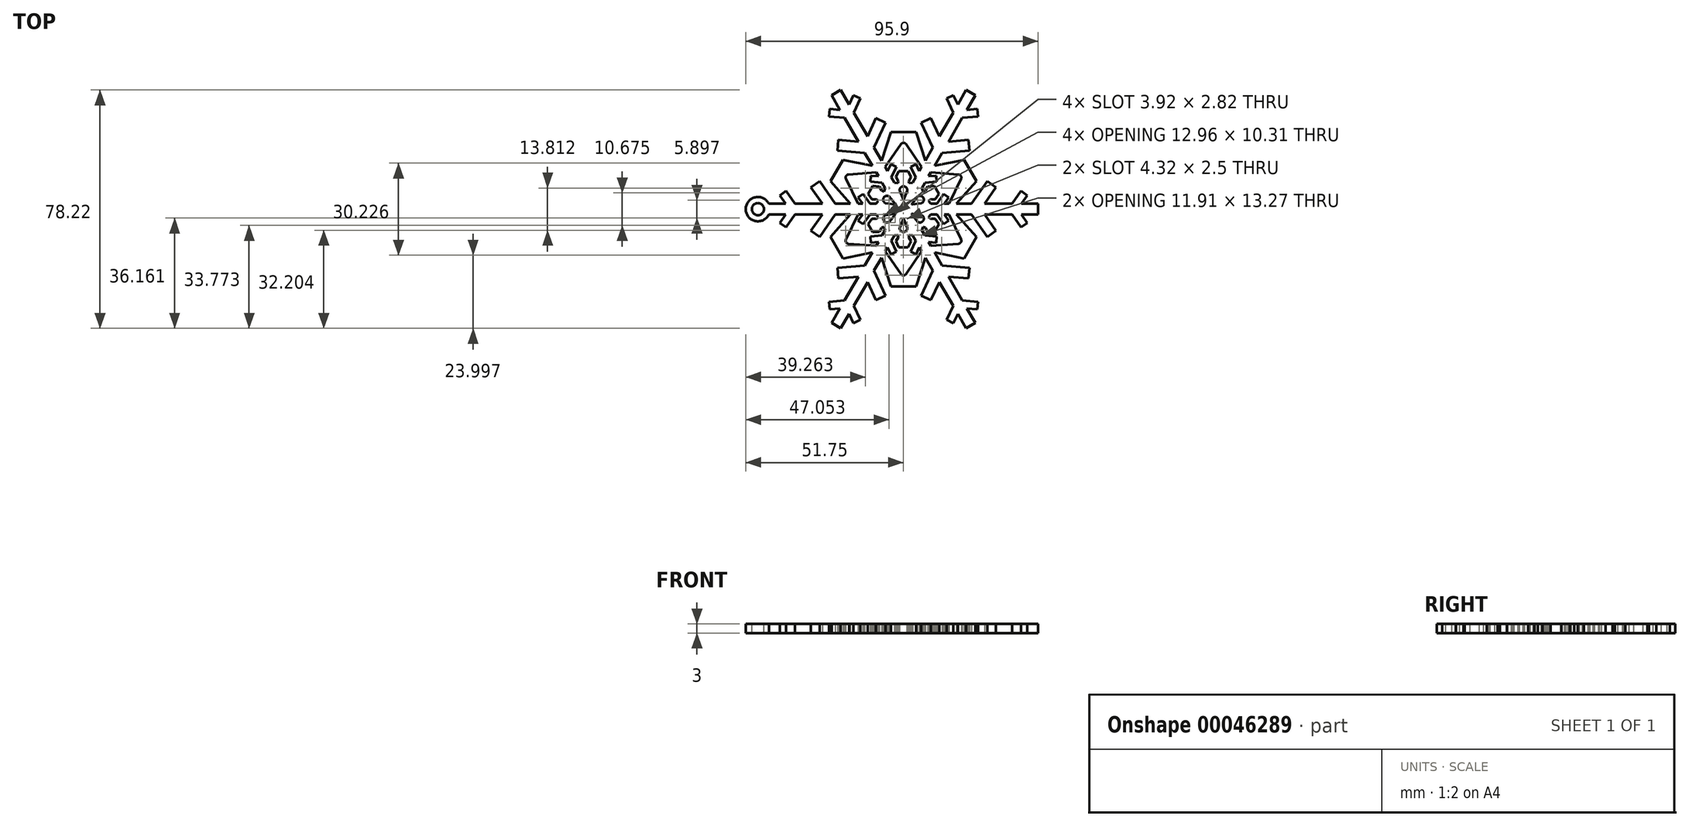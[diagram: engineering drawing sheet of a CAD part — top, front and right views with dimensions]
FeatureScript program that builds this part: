
annotation { "Feature Type Name" : "Feature", "Feature Type Description" : "" }
export const myFeature = defineFeature(function(context is Context, id is Id, definition is map)
    precondition{}
    {
        {
            var Q0;
            Q0=qCreatedBy(makeId("Top.planeOp"),FACE);
            var sketch = newSketch(context, id + "F0", { "sketchPlane" : qUnion([Q0])});
            skLineSegment(sketch, "E0.bottom", {"start": v(-43.7, 44.8) * mm, "end": v(41.1, 44.8) * mm});
            skLineSegment(sketch, "E0.top", {"start": v(-43.7, -40) * mm, "end": v(41.1, -40) * mm});
            skLineSegment(sketch, "E0.left", {"start": v(-43.7, 44.8) * mm, "end": v(-43.7, -40) * mm});
            skLineSegment(sketch, "E0.right", {"start": v(41.1, 44.8) * mm, "end": v(41.1, -40) * mm});
            skLineSegment(sketch, "E1", {"start": v(-44.15, 0) * mm, "end": v(-44.15, 1.75) * mm});
            skLineSegment(sketch, "E2", {"start": v(-44.15, 1.75) * mm, "end": v(-38.65, 1.75) * mm});
            skLineSegment(sketch, "E3", {"start": v(-38.65, 1.75) * mm, "end": v(-40.58, 4.5) * mm});
            skLineSegment(sketch, "E4", {"start": v(-40.58, 4.5) * mm, "end": v(-38.53, 5.94) * mm});
            skLineSegment(sketch, "E5", {"start": v(-38.53, 5.94) * mm, "end": v(-35.6, 1.75) * mm});
            skLineSegment(sketch, "E6", {"start": v(-35.6, 1.75) * mm, "end": v(-26.6, 1.75) * mm});
            skLineSegment(sketch, "E7", {"start": v(-26.6, 1.75) * mm, "end": v(-30.36, 7.13) * mm});
            skLineSegment(sketch, "E8", {"start": v(-30.36, 7.13) * mm, "end": v(-27.49, 9.13) * mm});
            skLineSegment(sketch, "E9", {"start": v(-27.49, 9.13) * mm, "end": v(-22.34, 1.75) * mm});
            skLineSegment(sketch, "E10", {"start": v(-22.34, 1.75) * mm, "end": v(-17.4, 1.75) * mm});
            skLineSegment(sketch, "E11", {"start": v(-14.94, 1.75) * mm, "end": v(-13.44, 1.75) * mm});
            skLineSegment(sketch, "E12", {"start": v(-13.44, 1.75) * mm, "end": v(-14.87, 3.8) * mm});
            skLineSegment(sketch, "E13", {"start": v(-14.87, 3.8) * mm, "end": v(-13.23, 4.94) * mm});
            skLineSegment(sketch, "E14", {"start": v(-13.23, 4.94) * mm, "end": v(-11, 1.75) * mm});
            skLineSegment(sketch, "E15", {"start": v(0, 0) * mm, "end": v(-44.15, 0) * mm, "construction": true});
            skLineSegment(sketch, "E16", {"start": v(-11, 1.75) * mm, "end": v(-8.98, 1.75) * mm});
            skLineSegment(sketch, "E17", {"start": v(0, 0) * mm, "end": v(-10.85, 6.27) * mm});
            skLineSegment(sketch, "E18", {"start": v(-8.98, 1.75) * mm, "end": v(-8.24, 2.67) * mm});
            skLineSegment(sketch, "E19", {"start": v(-8.24, 2.67) * mm, "end": v(-8.84, 3.15) * mm});
            skLineSegment(sketch, "E20", {"start": v(-8.84, 3.15) * mm, "end": v(-10.37, 3.15) * mm});
            skLineSegment(sketch, "E21", {"start": v(-10.37, 3.15) * mm, "end": v(-11.62, 4.94) * mm});
            skLineSegment(sketch, "E22", {"start": v(-11.62, 4.94) * mm, "end": v(-10.85, 6.27) * mm});
            skLineSegment(sketch, "E23", {"start": v(-10.85, 6.27) * mm, "end": v(-31.84, 18.38) * mm, "construction": true});
            skLineSegment(sketch, "E24", {"start": v(-23.98, 9.13) * mm, "end": v(-21.94, 12.67) * mm});
            skLineSegment(sketch, "E25", {"start": v(-14.94, 1.75) * mm, "end": v(-19.5, 11.26) * mm});
            skLineSegment(sketch, "E26", {"start": v(-23.98, 9.13) * mm, "end": v(-17.4, 1.75) * mm});
            skLineSegment(sketch, "E27", {"start": v(-21.94, 12.67) * mm, "end": v(-19.5, 11.26) * mm});
            skLineSegment(sketch, "E28.MirrorCS", {"start": v(0, 0) * mm, "end": v(-10.85, -6.27) * mm});
            skLineSegment(sketch, "E29.MirrorCS", {"start": v(-44.15, 0) * mm, "end": v(-44.15, -1.75) * mm});
            skLineSegment(sketch, "E30.MirrorCS", {"start": v(-14.94, -1.75) * mm, "end": v(-13.44, -1.75) * mm});
            skLineSegment(sketch, "E31.MirrorCS", {"start": v(-11.62, -4.94) * mm, "end": v(-10.85, -6.27) * mm});
            skLineSegment(sketch, "E32.MirrorCS", {"start": v(-14.87, -3.8) * mm, "end": v(-13.23, -4.94) * mm});
            skLineSegment(sketch, "E33.MirrorCS", {"start": v(-8.98, -1.75) * mm, "end": v(-8.24, -2.67) * mm});
            skLineSegment(sketch, "E34.MirrorCS", {"start": v(-8.84, -3.15) * mm, "end": v(-10.37, -3.15) * mm});
            skLineSegment(sketch, "E35.MirrorCS", {"start": v(-8.24, -2.67) * mm, "end": v(-8.84, -3.15) * mm});
            skLineSegment(sketch, "E36.MirrorCS", {"start": v(-14.94, -1.75) * mm, "end": v(-19.5, -11.26) * mm});
            skLineSegment(sketch, "E37.MirrorCS", {"start": v(-27.49, -9.13) * mm, "end": v(-22.34, -1.75) * mm});
            skLineSegment(sketch, "E38.MirrorCS", {"start": v(-21.94, -12.67) * mm, "end": v(-19.5, -11.26) * mm});
            skLineSegment(sketch, "E39.MirrorCS", {"start": v(-23.98, -9.13) * mm, "end": v(-21.94, -12.67) * mm});
            skLineSegment(sketch, "E40.MirrorCS", {"start": v(-11, -1.75) * mm, "end": v(-8.98, -1.75) * mm});
            skLineSegment(sketch, "E41.MirrorCS", {"start": v(-38.53, -5.94) * mm, "end": v(-35.6, -1.75) * mm});
            skLineSegment(sketch, "E42.MirrorCS", {"start": v(-40.58, -4.5) * mm, "end": v(-38.53, -5.94) * mm});
            skLineSegment(sketch, "E43.MirrorCS", {"start": v(-38.65, -1.75) * mm, "end": v(-40.58, -4.5) * mm});
            skLineSegment(sketch, "E44.MirrorCS", {"start": v(-44.15, -1.75) * mm, "end": v(-38.65, -1.75) * mm});
            skLineSegment(sketch, "E45.MirrorCS", {"start": v(-23.98, -9.13) * mm, "end": v(-17.4, -1.75) * mm});
            skLineSegment(sketch, "E46.MirrorCS", {"start": v(-30.36, -7.13) * mm, "end": v(-27.49, -9.13) * mm});
            skLineSegment(sketch, "E47.MirrorCS", {"start": v(-26.6, -1.75) * mm, "end": v(-30.36, -7.13) * mm});
            skLineSegment(sketch, "E48.MirrorCS", {"start": v(-35.6, -1.75) * mm, "end": v(-26.6, -1.75) * mm});
            skLineSegment(sketch, "E49.MirrorCS", {"start": v(-22.34, -1.75) * mm, "end": v(-17.4, -1.75) * mm});
            skLineSegment(sketch, "E50.MirrorCS", {"start": v(-13.44, -1.75) * mm, "end": v(-14.87, -3.8) * mm});
            skLineSegment(sketch, "E51.MirrorCS", {"start": v(-10.37, -3.15) * mm, "end": v(-11.62, -4.94) * mm});
            skLineSegment(sketch, "E52.MirrorCS", {"start": v(-13.23, -4.94) * mm, "end": v(-11, -1.75) * mm});
            skSolve(sketch);
        }
        {
            var Q0;
            Q0=makeQuery(id+"F0.imprint","IMPRINT",FACE,{"disambiguationData":[TD([[makeQuery(id+"F0.imprint","IMPRINT",EDGE,{"derivedFrom":sQuery(id+"F0.wireOp",EDGE,"E1")}),-1.0]])]});
            var Q1;
            {var subQ0=sQuery(id+"F0.wireOp",EDGE,"E3");Q1=makeQuery(id+"F0.imprint","IMPRINT",FACE,{"disambiguationData":[TD([[makeQuery(id+"F0.imprint","IMPRINT",EDGE,{"derivedFrom":subQ0}),-1.0]])]});}
            extrude(context, id + "F1", {"entities" : qUnion([Q0, Q1]), "endBound" : BoundingType.SYMMETRIC, "depth" : 3 * mm});
        }
        {
            var Q0;
            Q0=qCreatedBy(makeId("Right.planeOp"),FACE);
            var sketch = newSketch(context, id + "F2", { "sketchPlane" : qUnion([Q0])});
            skLineSegment(sketch, "E53", {"start": v(0, 0) * mm, "end": v(0, -43.45) * mm, "construction": true});
            skSolve(sketch);
        }
        {
            var Q0;
            Q0=makeQuery(id+"F1.opExtrude","SWEPT_BODY",BODY,{"disambiguationData":[OSD([sQuery(id+"F0.wireOp",EDGE,"E1"),sQuery(id+"F0.wireOp",EDGE,"E2"),sQuery(id+"F0.wireOp",EDGE,"E3"),sQuery(id+"F0.wireOp",EDGE,"E4"),sQuery(id+"F0.wireOp",EDGE,"E5"),sQuery(id+"F0.wireOp",EDGE,"E6"),sQuery(id+"F0.wireOp",EDGE,"E7"),sQuery(id+"F0.wireOp",EDGE,"E8"),sQuery(id+"F0.wireOp",EDGE,"E9"),sQuery(id+"F0.wireOp",EDGE,"E10"),sQuery(id+"F0.wireOp",EDGE,"189a7a4e-f39c-4bfd-b122-43a29ca94680"),sQuery(id+"F0.wireOp",EDGE,"67050dc1-3990-4a49-9707-dffdccfb30a0"),sQuery(id+"F0.wireOp",EDGE,"437a0215-fb6c-4063-ad75-b84b83856d58"),sQuery(id+"F0.wireOp",EDGE,"E11"),sQuery(id+"F0.wireOp",EDGE,"E12"),sQuery(id+"F0.wireOp",EDGE,"E13"),sQuery(id+"F0.wireOp",EDGE,"E14"),sQuery(id+"F0.wireOp",EDGE,"5e9898c1-a996-4e9f-834a-20b7154747a1"),sQuery(id+"F0.wireOp",EDGE,"4f175b08-8b9f-4015-be58-81c3dce13333"),sQuery(id+"F0.wireOp",EDGE,"3166d6ec-2b74-46b0-8a25-8ff819b97b050.MirrorCS"),sQuery(id+"F0.wireOp",EDGE,"3166d6ec-2b74-46b0-8a25-8ff819b97b051.MirrorCS"),sQuery(id+"F0.wireOp",EDGE,"3166d6ec-2b74-46b0-8a25-8ff819b97b052.MirrorCS"),sQuery(id+"F0.wireOp",EDGE,"3166d6ec-2b74-46b0-8a25-8ff819b97b053.MirrorCS"),sQuery(id+"F0.wireOp",EDGE,"3166d6ec-2b74-46b0-8a25-8ff819b97b054.MirrorCS"),sQuery(id+"F0.wireOp",EDGE,"3166d6ec-2b74-46b0-8a25-8ff819b97b055.MirrorCS"),sQuery(id+"F0.wireOp",EDGE,"3166d6ec-2b74-46b0-8a25-8ff819b97b056.MirrorCS"),sQuery(id+"F0.wireOp",EDGE,"3166d6ec-2b74-46b0-8a25-8ff819b97b057.MirrorCS"),sQuery(id+"F0.wireOp",EDGE,"3166d6ec-2b74-46b0-8a25-8ff819b97b058.MirrorCS"),sQuery(id+"F0.wireOp",EDGE,"3166d6ec-2b74-46b0-8a25-8ff819b97b059.MirrorCS"),sQuery(id+"F0.wireOp",EDGE,"3166d6ec-2b74-46b0-8a25-8ff819b97b0510.MirrorCS"),sQuery(id+"F0.wireOp",EDGE,"3166d6ec-2b74-46b0-8a25-8ff819b97b0511.MirrorCS"),sQuery(id+"F0.wireOp",EDGE,"3166d6ec-2b74-46b0-8a25-8ff819b97b0512.MirrorCS"),sQuery(id+"F0.wireOp",EDGE,"3166d6ec-2b74-46b0-8a25-8ff819b97b0513.MirrorCS"),sQuery(id+"F0.wireOp",EDGE,"3166d6ec-2b74-46b0-8a25-8ff819b97b0514.MirrorCS"),sQuery(id+"F0.wireOp",EDGE,"3166d6ec-2b74-46b0-8a25-8ff819b97b0515.MirrorCS"),sQuery(id+"F0.wireOp",EDGE,"3166d6ec-2b74-46b0-8a25-8ff819b97b0516.MirrorCS"),sQuery(id+"F0.wireOp",EDGE,"3166d6ec-2b74-46b0-8a25-8ff819b97b0517.MirrorCS"),sQuery(id+"F0.wireOp",EDGE,"3166d6ec-2b74-46b0-8a25-8ff819b97b0518.MirrorCS")])]});
            var Q1;
            Q1=sQuery(id+"F2.wireOp",EDGE,"E53");
            circularPattern(context, id + "F3", {"operationType" : NewBodyOperationType.ADD, "entities" : qUnion([Q0]), "axis" : qUnion([Q1]), "angle" : 60 * degree, "instanceCount" : 6});
        }
        {
            var Q0;
            {var subQ0=makeQuery(id+"F1.opExtrude","CAP_FACE",FACE,{"disambiguationData":[OSD([sQuery(id+"F0.wireOp",EDGE,"E1"),sQuery(id+"F0.wireOp",EDGE,"E2"),sQuery(id+"F0.wireOp",EDGE,"E3"),sQuery(id+"F0.wireOp",EDGE,"E4"),sQuery(id+"F0.wireOp",EDGE,"E5"),sQuery(id+"F0.wireOp",EDGE,"E6"),sQuery(id+"F0.wireOp",EDGE,"E7"),sQuery(id+"F0.wireOp",EDGE,"E8"),sQuery(id+"F0.wireOp",EDGE,"E9"),sQuery(id+"F0.wireOp",EDGE,"E10"),sQuery(id+"F0.wireOp",EDGE,"189a7a4e-f39c-4bfd-b122-43a29ca94680"),sQuery(id+"F0.wireOp",EDGE,"67050dc1-3990-4a49-9707-dffdccfb30a0"),sQuery(id+"F0.wireOp",EDGE,"437a0215-fb6c-4063-ad75-b84b83856d58"),sQuery(id+"F0.wireOp",EDGE,"E11"),sQuery(id+"F0.wireOp",EDGE,"E12"),sQuery(id+"F0.wireOp",EDGE,"E13"),sQuery(id+"F0.wireOp",EDGE,"E14"),sQuery(id+"F0.wireOp",EDGE,"E16"),sQuery(id+"F0.wireOp",EDGE,"E17"),sQuery(id+"F0.wireOp",EDGE,"E18"),sQuery(id+"F0.wireOp",EDGE,"E19"),sQuery(id+"F0.wireOp",EDGE,"E20"),sQuery(id+"F0.wireOp",EDGE,"E21"),sQuery(id+"F0.wireOp",EDGE,"E22"),sQuery(id+"F0.wireOp",EDGE,"0c32c283-354d-45ec-8926-575daeb4bd260.MirrorCS"),sQuery(id+"F0.wireOp",EDGE,"0c32c283-354d-45ec-8926-575daeb4bd261.MirrorCS"),sQuery(id+"F0.wireOp",EDGE,"0c32c283-354d-45ec-8926-575daeb4bd262.MirrorCS"),sQuery(id+"F0.wireOp",EDGE,"0c32c283-354d-45ec-8926-575daeb4bd263.MirrorCS"),sQuery(id+"F0.wireOp",EDGE,"0c32c283-354d-45ec-8926-575daeb4bd264.MirrorCS"),sQuery(id+"F0.wireOp",EDGE,"0c32c283-354d-45ec-8926-575daeb4bd265.MirrorCS"),sQuery(id+"F0.wireOp",EDGE,"0c32c283-354d-45ec-8926-575daeb4bd266.MirrorCS"),sQuery(id+"F0.wireOp",EDGE,"0c32c283-354d-45ec-8926-575daeb4bd267.MirrorCS"),sQuery(id+"F0.wireOp",EDGE,"0c32c283-354d-45ec-8926-575daeb4bd268.MirrorCS"),sQuery(id+"F0.wireOp",EDGE,"0c32c283-354d-45ec-8926-575daeb4bd269.MirrorCS"),sQuery(id+"F0.wireOp",EDGE,"0c32c283-354d-45ec-8926-575daeb4bd2610.MirrorCS"),sQuery(id+"F0.wireOp",EDGE,"0c32c283-354d-45ec-8926-575daeb4bd2611.MirrorCS"),sQuery(id+"F0.wireOp",EDGE,"0c32c283-354d-45ec-8926-575daeb4bd2612.MirrorCS"),sQuery(id+"F0.wireOp",EDGE,"0c32c283-354d-45ec-8926-575daeb4bd2613.MirrorCS"),sQuery(id+"F0.wireOp",EDGE,"0c32c283-354d-45ec-8926-575daeb4bd2614.MirrorCS"),sQuery(id+"F0.wireOp",EDGE,"0c32c283-354d-45ec-8926-575daeb4bd2615.MirrorCS"),sQuery(id+"F0.wireOp",EDGE,"0c32c283-354d-45ec-8926-575daeb4bd2616.MirrorCS"),sQuery(id+"F0.wireOp",EDGE,"0c32c283-354d-45ec-8926-575daeb4bd2617.MirrorCS"),sQuery(id+"F0.wireOp",EDGE,"0c32c283-354d-45ec-8926-575daeb4bd2618.MirrorCS"),sQuery(id+"F0.wireOp",EDGE,"0c32c283-354d-45ec-8926-575daeb4bd2619.MirrorCS"),sQuery(id+"F0.wireOp",EDGE,"0c32c283-354d-45ec-8926-575daeb4bd2620.MirrorCS"),sQuery(id+"F0.wireOp",EDGE,"0c32c283-354d-45ec-8926-575daeb4bd2621.MirrorCS"),sQuery(id+"F0.wireOp",EDGE,"0c32c283-354d-45ec-8926-575daeb4bd2622.MirrorCS"),sQuery(id+"F0.wireOp",EDGE,"0c32c283-354d-45ec-8926-575daeb4bd2623.MirrorCS")])],"isStart":false});Q0=makeQuery(id+"F3.boolean.opBoolean","MERGE",FACE,{"derivedFrom":[subQ0,makeQuery(id+"F3.opPattern","COPY",FACE,{"derivedFrom":subQ0,"instanceName":"1"}),makeQuery(id+"F3.opPattern","COPY",FACE,{"derivedFrom":subQ0,"instanceName":"2"}),makeQuery(id+"F3.opPattern","COPY",FACE,{"derivedFrom":subQ0,"instanceName":"3"}),makeQuery(id+"F3.opPattern","COPY",FACE,{"derivedFrom":subQ0,"instanceName":"4"}),makeQuery(id+"F3.opPattern","COPY",FACE,{"derivedFrom":subQ0,"instanceName":"5"})]});}
            var sketch = newSketch(context, id + "F4", { "sketchPlane" : qUnion([Q0])});
            skLineSegment(sketch, "E54", {"start": v(0, 0) * mm, "end": v(-10.85, 6.27) * mm, "construction": true});
            skLineSegment(sketch, "E55", {"start": v(-6.5, 3.75) * mm, "end": v(-2.6, 1.5) * mm, "construction": true});
            skLineSegment(sketch, "E56", {"start": v(-5.87, 1.94) * mm, "end": v(-2.6, 1.5) * mm});
            skLineSegment(sketch, "E57.MirrorCS", {"start": v(-4.62, 4.1) * mm, "end": v(-2.6, 1.5) * mm});
            skLineSegment(sketch, "E58", {"start": v(-5.87, 1.94) * mm, "end": v(-4.62, 4.1) * mm, "construction": true});
            skArc(sketch, "E59", {"start": v(-4.62, 4.1) * mm, "mid": v(-6.5, 3.75) * mm, "end": v(-5.87, 1.94) * mm});
            skSolve(sketch);
        }
        {
            var Q0;
            Q0=makeQuery(id+"F4.imprint","IMPRINT",FACE,{"disambiguationData":[TD([[makeQuery(id+"F4.imprint","IMPRINT",EDGE,{"derivedFrom":sQuery(id+"F4.wireOp",EDGE,"980073ca-cf30-472a-b92e-9ee7ff5da41c")}),1.0]])]});
            var Q1;
            Q1=makeQuery(id+"F4.imprint","IMPRINT",FACE,{"disambiguationData":[TD([[makeQuery(id+"F4.imprint","IMPRINT",EDGE,{"derivedFrom":sQuery(id+"F4.wireOp",EDGE,"E56")}),1.0]])]});
            extrude(context, id + "F5", {"entities" : qUnion([Q0, Q1]), "operationType" : NewBodyOperationType.REMOVE, "endBound" : BoundingType.UP_TO_NEXT, "oppositeDirection" : true, "depth" : 25 * mm});
        }
        {
            var Q0;
            Q0=makeQuery(id+"F5.boolean.opBoolean","COPY",EDGE,{"derivedFrom":makeQuery(id+"F5.opExtrude","SWEPT_EDGE",EDGE,{"disambiguationData":[OSD([sQuery(id+"F4.wireOp",EDGE,"E56"),sQuery(id+"F4.wireOp",EDGE,"E57.MirrorCS")])]})});
            fillet(context, id + "F6", {"entities" : qUnion([Q0]), "radius" : 0.1 * mm, "tangentPropagation" : true, "allowEdgeOverflow" : false});
        }
        {
            var Q0;
            Q0=makeQuery(id+"F5.boolean.opBoolean","COPY",FACE,{"derivedFrom":makeQuery(id+"F5.opExtrude","SWEPT_FACE",FACE,{"disambiguationData":[OSD([sQuery(id+"F4.wireOp",EDGE,"E59")])]})});
            var Q1;
            Q1=makeQuery(id+"F5.boolean.opBoolean","COPY",FACE,{"derivedFrom":makeQuery(id+"F5.opExtrude","SWEPT_FACE",FACE,{"disambiguationData":[OSD([sQuery(id+"F4.wireOp",EDGE,"E56")])]})});
            var Q2;
            Q2=makeQuery(id+"F5.boolean.opBoolean","COPY",FACE,{"derivedFrom":makeQuery(id+"F5.opExtrude","SWEPT_FACE",FACE,{"disambiguationData":[OSD([sQuery(id+"F4.wireOp",EDGE,"E57.MirrorCS")])]})});
            var Q3;
            Q3=makeQuery(id+"F6.opFillet","BLEND_FACE",FACE,{"disambiguationData":[OSD([sQuery(id+"F4.wireOp",EDGE,"E56"),sQuery(id+"F4.wireOp",EDGE,"E57.MirrorCS")])]});
            var Q4;
            Q4=sQuery(id+"F2.wireOp",EDGE,"E53");
            circularPattern(context, id + "F7", {"faces" : qUnion([Q0, Q1, Q2, Q3]), "axis" : qUnion([Q4]), "angle" : 60 * degree, "instanceCount" : 6, "patternType" : PatternType.FACE});
        }
        {
            var Q0;
            {var subQ0=makeQuery(id+"F1.opExtrude","CAP_FACE",FACE,{"disambiguationData":[OSD([sQuery(id+"F0.wireOp",EDGE,"E1"),sQuery(id+"F0.wireOp",EDGE,"E2"),sQuery(id+"F0.wireOp",EDGE,"E3"),sQuery(id+"F0.wireOp",EDGE,"E4"),sQuery(id+"F0.wireOp",EDGE,"E5"),sQuery(id+"F0.wireOp",EDGE,"E6"),sQuery(id+"F0.wireOp",EDGE,"E7"),sQuery(id+"F0.wireOp",EDGE,"E8"),sQuery(id+"F0.wireOp",EDGE,"E9"),sQuery(id+"F0.wireOp",EDGE,"E10"),sQuery(id+"F0.wireOp",EDGE,"189a7a4e-f39c-4bfd-b122-43a29ca94680"),sQuery(id+"F0.wireOp",EDGE,"67050dc1-3990-4a49-9707-dffdccfb30a0"),sQuery(id+"F0.wireOp",EDGE,"437a0215-fb6c-4063-ad75-b84b83856d58"),sQuery(id+"F0.wireOp",EDGE,"E11"),sQuery(id+"F0.wireOp",EDGE,"E12"),sQuery(id+"F0.wireOp",EDGE,"E13"),sQuery(id+"F0.wireOp",EDGE,"E14"),sQuery(id+"F0.wireOp",EDGE,"E16"),sQuery(id+"F0.wireOp",EDGE,"E17"),sQuery(id+"F0.wireOp",EDGE,"E18"),sQuery(id+"F0.wireOp",EDGE,"E19"),sQuery(id+"F0.wireOp",EDGE,"E20"),sQuery(id+"F0.wireOp",EDGE,"E21"),sQuery(id+"F0.wireOp",EDGE,"E22"),sQuery(id+"F0.wireOp",EDGE,"0c32c283-354d-45ec-8926-575daeb4bd260.MirrorCS"),sQuery(id+"F0.wireOp",EDGE,"0c32c283-354d-45ec-8926-575daeb4bd261.MirrorCS"),sQuery(id+"F0.wireOp",EDGE,"0c32c283-354d-45ec-8926-575daeb4bd262.MirrorCS"),sQuery(id+"F0.wireOp",EDGE,"0c32c283-354d-45ec-8926-575daeb4bd263.MirrorCS"),sQuery(id+"F0.wireOp",EDGE,"0c32c283-354d-45ec-8926-575daeb4bd264.MirrorCS"),sQuery(id+"F0.wireOp",EDGE,"0c32c283-354d-45ec-8926-575daeb4bd265.MirrorCS"),sQuery(id+"F0.wireOp",EDGE,"0c32c283-354d-45ec-8926-575daeb4bd266.MirrorCS"),sQuery(id+"F0.wireOp",EDGE,"0c32c283-354d-45ec-8926-575daeb4bd267.MirrorCS"),sQuery(id+"F0.wireOp",EDGE,"0c32c283-354d-45ec-8926-575daeb4bd268.MirrorCS"),sQuery(id+"F0.wireOp",EDGE,"0c32c283-354d-45ec-8926-575daeb4bd269.MirrorCS"),sQuery(id+"F0.wireOp",EDGE,"0c32c283-354d-45ec-8926-575daeb4bd2610.MirrorCS"),sQuery(id+"F0.wireOp",EDGE,"0c32c283-354d-45ec-8926-575daeb4bd2611.MirrorCS"),sQuery(id+"F0.wireOp",EDGE,"0c32c283-354d-45ec-8926-575daeb4bd2612.MirrorCS"),sQuery(id+"F0.wireOp",EDGE,"0c32c283-354d-45ec-8926-575daeb4bd2613.MirrorCS"),sQuery(id+"F0.wireOp",EDGE,"0c32c283-354d-45ec-8926-575daeb4bd2614.MirrorCS"),sQuery(id+"F0.wireOp",EDGE,"0c32c283-354d-45ec-8926-575daeb4bd2615.MirrorCS"),sQuery(id+"F0.wireOp",EDGE,"0c32c283-354d-45ec-8926-575daeb4bd2616.MirrorCS"),sQuery(id+"F0.wireOp",EDGE,"0c32c283-354d-45ec-8926-575daeb4bd2617.MirrorCS"),sQuery(id+"F0.wireOp",EDGE,"0c32c283-354d-45ec-8926-575daeb4bd2618.MirrorCS"),sQuery(id+"F0.wireOp",EDGE,"0c32c283-354d-45ec-8926-575daeb4bd2619.MirrorCS"),sQuery(id+"F0.wireOp",EDGE,"0c32c283-354d-45ec-8926-575daeb4bd2620.MirrorCS"),sQuery(id+"F0.wireOp",EDGE,"0c32c283-354d-45ec-8926-575daeb4bd2621.MirrorCS"),sQuery(id+"F0.wireOp",EDGE,"0c32c283-354d-45ec-8926-575daeb4bd2622.MirrorCS"),sQuery(id+"F0.wireOp",EDGE,"0c32c283-354d-45ec-8926-575daeb4bd2623.MirrorCS")])],"isStart":false});Q0=makeQuery(id+"F3.boolean.opBoolean","MERGE",FACE,{"derivedFrom":[subQ0,makeQuery(id+"F3.opPattern","COPY",FACE,{"derivedFrom":subQ0,"instanceName":"1"}),makeQuery(id+"F3.opPattern","COPY",FACE,{"derivedFrom":subQ0,"instanceName":"2"}),makeQuery(id+"F3.opPattern","COPY",FACE,{"derivedFrom":subQ0,"instanceName":"3"}),makeQuery(id+"F3.opPattern","COPY",FACE,{"derivedFrom":subQ0,"instanceName":"4"}),makeQuery(id+"F3.opPattern","COPY",FACE,{"derivedFrom":subQ0,"instanceName":"5"})]});}
            var sketch = newSketch(context, id + "F8", { "sketchPlane" : qUnion([Q0])});
            skArc(sketch, "E60", {"start": v(-44.15, 1.75) * mm, "mid": v(-51.75, 0) * mm, "end": v(-44.15, -1.75) * mm});
            skCircle(sketch, "E61", {"center": v(-47.75, 0) * mm, "radius": 2 * mm});
            skSolve(sketch);
        }
        {
            var Q0;
            Q0=makeQuery(id+"F8.imprint","IMPRINT",FACE,{"disambiguationData":[TD([[makeQuery(id+"F8.imprint","IMPRINT",EDGE,{"derivedFrom":sQuery(id+"F8.wireOp",EDGE,"E60")}),1.0]])]});
            extrude(context, id + "F9", {"entities" : qUnion([Q0]), "operationType" : NewBodyOperationType.ADD, "oppositeDirection" : true, "depth" : 3 * mm});
        }
        {
            var Q0;
            Q0=makeQuery(id+"F3.boolean.opBoolean","MERGE",EDGE,{"derivedFrom":[makeQuery(id+"F1.opExtrude","SWEPT_EDGE",EDGE,{"disambiguationData":[OSD([sQuery(id+"F0.wireOp",EDGE,"E25"),sQuery(id+"F0.wireOp",EDGE,"E27")])]}),makeQuery(id+"F3.opPattern","COPY",EDGE,{"derivedFrom":makeQuery(id+"F1.opExtrude","SWEPT_EDGE",EDGE,{"disambiguationData":[OSD([sQuery(id+"F0.wireOp",EDGE,"E36.MirrorCS"),sQuery(id+"F0.wireOp",EDGE,"E38.MirrorCS")])]}),"instanceName":"1"})]});
            var Q1;
            Q1=makeQuery(id+"F3.boolean.opBoolean","MERGE",EDGE,{"derivedFrom":[makeQuery(id+"F1.opExtrude","SWEPT_EDGE",EDGE,{"disambiguationData":[OSD([sQuery(id+"F0.wireOp",EDGE,"E36.MirrorCS"),sQuery(id+"F0.wireOp",EDGE,"E38.MirrorCS")])]}),makeQuery(id+"F3.opPattern","COPY",EDGE,{"derivedFrom":makeQuery(id+"F1.opExtrude","SWEPT_EDGE",EDGE,{"disambiguationData":[OSD([sQuery(id+"F0.wireOp",EDGE,"E25"),sQuery(id+"F0.wireOp",EDGE,"E27")])]}),"instanceName":"5"})]});
            var Q2;
            Q2=makeQuery(id+"F3.boolean.opBoolean","MERGE",EDGE,{"derivedFrom":[makeQuery(id+"F3.opPattern","COPY",EDGE,{"derivedFrom":makeQuery(id+"F1.opExtrude","SWEPT_EDGE",EDGE,{"disambiguationData":[OSD([sQuery(id+"F0.wireOp",EDGE,"E25"),sQuery(id+"F0.wireOp",EDGE,"E27")])]}),"instanceName":"4"}),makeQuery(id+"F3.opPattern","COPY",EDGE,{"derivedFrom":makeQuery(id+"F1.opExtrude","SWEPT_EDGE",EDGE,{"disambiguationData":[OSD([sQuery(id+"F0.wireOp",EDGE,"E36.MirrorCS"),sQuery(id+"F0.wireOp",EDGE,"E38.MirrorCS")])]}),"instanceName":"5"})]});
            var Q3;
            Q3=makeQuery(id+"F3.boolean.opBoolean","MERGE",EDGE,{"derivedFrom":[makeQuery(id+"F3.opPattern","COPY",EDGE,{"derivedFrom":makeQuery(id+"F1.opExtrude","SWEPT_EDGE",EDGE,{"disambiguationData":[OSD([sQuery(id+"F0.wireOp",EDGE,"E25"),sQuery(id+"F0.wireOp",EDGE,"E27")])]}),"instanceName":"3"}),makeQuery(id+"F3.opPattern","COPY",EDGE,{"derivedFrom":makeQuery(id+"F1.opExtrude","SWEPT_EDGE",EDGE,{"disambiguationData":[OSD([sQuery(id+"F0.wireOp",EDGE,"E36.MirrorCS"),sQuery(id+"F0.wireOp",EDGE,"E38.MirrorCS")])]}),"instanceName":"4"})]});
            var Q4;
            Q4=makeQuery(id+"F3.boolean.opBoolean","MERGE",EDGE,{"derivedFrom":[makeQuery(id+"F3.opPattern","COPY",EDGE,{"derivedFrom":makeQuery(id+"F1.opExtrude","SWEPT_EDGE",EDGE,{"disambiguationData":[OSD([sQuery(id+"F0.wireOp",EDGE,"E25"),sQuery(id+"F0.wireOp",EDGE,"E27")])]}),"instanceName":"1"}),makeQuery(id+"F3.opPattern","COPY",EDGE,{"derivedFrom":makeQuery(id+"F1.opExtrude","SWEPT_EDGE",EDGE,{"disambiguationData":[OSD([sQuery(id+"F0.wireOp",EDGE,"E36.MirrorCS"),sQuery(id+"F0.wireOp",EDGE,"E38.MirrorCS")])]}),"instanceName":"2"})]});
            var Q5;
            Q5=makeQuery(id+"F3.boolean.opBoolean","MERGE",EDGE,{"derivedFrom":[makeQuery(id+"F3.opPattern","COPY",EDGE,{"derivedFrom":makeQuery(id+"F1.opExtrude","SWEPT_EDGE",EDGE,{"disambiguationData":[OSD([sQuery(id+"F0.wireOp",EDGE,"E25"),sQuery(id+"F0.wireOp",EDGE,"E27")])]}),"instanceName":"2"}),makeQuery(id+"F3.opPattern","COPY",EDGE,{"derivedFrom":makeQuery(id+"F1.opExtrude","SWEPT_EDGE",EDGE,{"disambiguationData":[OSD([sQuery(id+"F0.wireOp",EDGE,"E36.MirrorCS"),sQuery(id+"F0.wireOp",EDGE,"E38.MirrorCS")])]}),"instanceName":"3"})]});
            fillet(context, id + "F10", {"entities" : qUnion([Q0, Q1, Q2, Q3, Q4, Q5]), "radius" : 1 * mm, "tangentPropagation" : true, "allowEdgeOverflow" : false});
        }
    });
